# Revit family: AM 50
name_source: partatom
category: Mechanical Equipment
units: mm (PartAtom-declared; Revit-internal decimal feet)

## family parameters
Always vertical = No
Classification = None
Cut with Voids When Loaded = No
OmniClass Number = 23.75.00.00
OmniClass Title = Climate Control (HVAC)
Part Type = Normal
Room Calculation Point = No
Round Connector Dimension = Use Diameter
Shared = No
Work Plane-Based = No

## types (1)
- AM 50
    Electrical connection = 1 ~ 230 V / N / PE / 50 Hz
    Manufacturer = Airmaster A/S
    Max. flow rate 25 dB(A) with ePM10 50% filters = 15 m³
    Max. flow rate 30 dB(A) with ePM10 50% filters = 30 m³
    Max. flow rate 35 dB(A) with ePM10 50% filters = 28 m³
    Max. flow rate 40 dB(A) with ePM10 50% filters = 37 m³
    Max. flow rate 45 dB(A) with ePM10 50% filters = 46 m³
    Max. flow rate 50 dB(A) with ePM10 50% filters = 59 m³
    Model = AM 50
    Nominal current,Cooling = 2,17 A
    Phase 1 - Max Current = 2,17 A
    Phase 1 - Max Power Consumption = 500 W
    URL = www.airmaster-as.com
    Wall Thikness = 250 mm
    Weight (Standard Unit) = 9.1

## geometry (parser evidence)
native form markers: Sweep x6
no freeform markers — native parametric forms only
